# Revit family: D SONNIGER - HEATER - MIX 1, MIX 2
name_source: partatom
category: Wyposażenie mechaniczne
revit_build: Autodesk Revit 2018 (Build: 20170927_1515(x64)
units: mm (PartAtom-declared; Revit-internal decimal feet)

## family parameters
Klasyfikacja = Brak
Obiekt nadrzędny = Powierzchnia
Punkt obliczania pomieszczeń = Nie
Tnij formami wycięć po wczytaniu = Nie
Typ części = Normalny
Współdzielony = Nie
Wymiar okrągłego złącza = Użyj średnicy

## types (2) — shared parameters
Autor = www.archispace.com
Betriebsspannung = 230 V
Domyślna rzędna = 1219.200 mm
Material = 230,230,230
Maximale Montagehöhe = 15.000 mm
Maximales Arbeitsfeld = 380 m²
Minimale Montagehöhe = 9.000 mm
Minimales Arbeitsfeld = 200 m²
Motor IP = IP54
O = 130.000 mm
Producent = SONNIGER Polska Sp. z o.o. Sp. k.
zero-valued in all types: Arbeitsniveau

## per-type parameters (varying)
| type | Gewicht / befüllt | Gewicht / unbefüllt | H | Lärmpegel | Maximale Luftleistung | Model | Motordrehzahl | Motorstärke | O1 | Opis | S g | W g |
| MIX 1 - Wandmontage | 9.20 kg | 9.20 kg | 13536.341 mm | I. Stufe 36 dB / II. Stufe 44 dB / III. Stufe 54 dB Geschwindigkeit | 4800.0 m³/h | Mix 1 | 1350 | 250 W | Tak | Lufterhitzer Heater MIX 1 | 19500.000 mm | 19500.000 mm |
| MIX 2 - Wandmontage | 15.80 kg | 15.80 kg | 16560.341 mm | I. Stufe 31 dB / II. Stufe 42 dB / III. Stufe 49 dB Geschwindigkeit | 7200.0 m³/h | Mix 2 | 1380 | 520 W | Nie | Lufterhitzer Heater MIX 2 | 21200.000 mm | 21200.000 mm |
